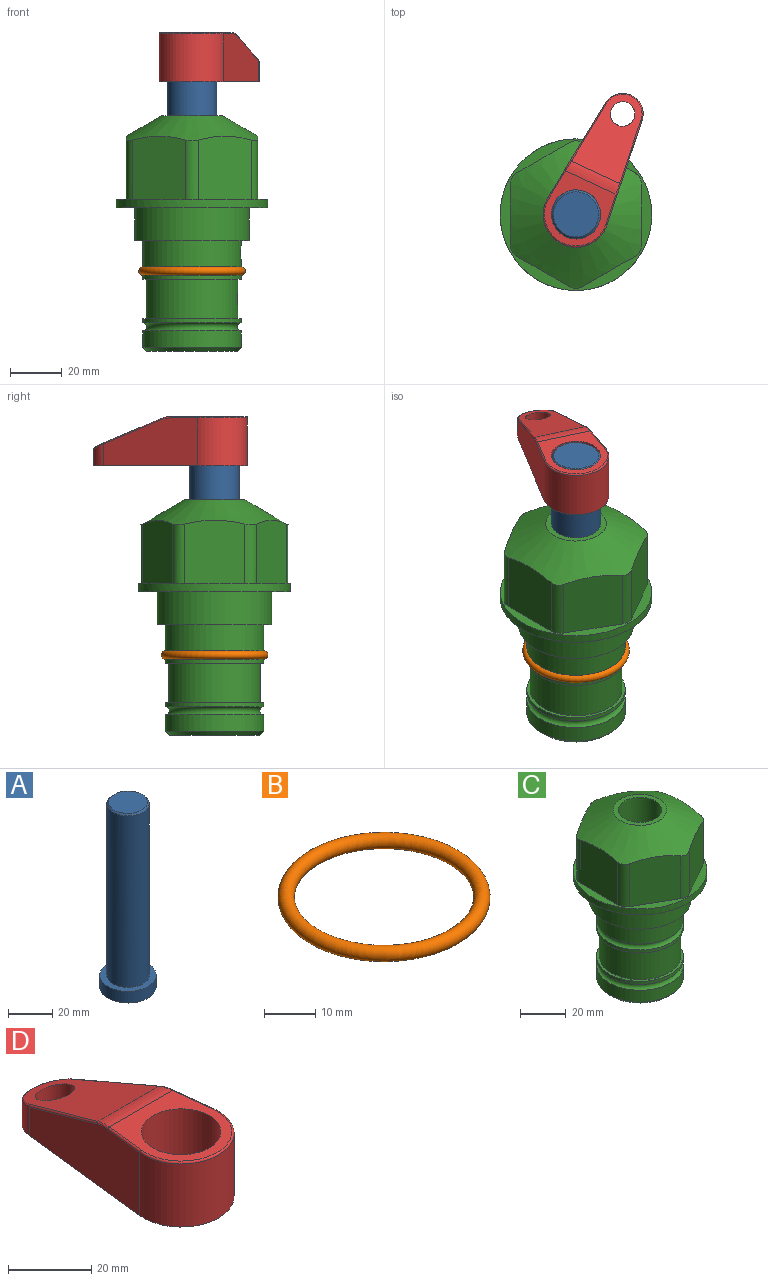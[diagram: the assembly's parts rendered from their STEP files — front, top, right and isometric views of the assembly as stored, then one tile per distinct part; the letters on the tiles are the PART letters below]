
ASSEMBLY  parts=4 mates=2
PART A: 6 faces, bbox 25.4x25.4x101.6 mm
  f0: plane 17.46x17.46mm, normal (0,0,1), area 239.5mm2, adj f5
  f1: plane 25.4x25.4mm, normal (0,0,-1), area 506.7mm2, adj f2
  f2: cylinder r=12.7mm len=25.4mm, axis (0,0,1), area 506.7mm2, adj f1,f3
  f3: plane 25.4x25.4mm, normal (0,0,1), area 221.7mm2, adj f2,f4
  f4: cylinder r=9.53mm len=94.46mm, axis (0,0,1), area 5653mm2, adj f3,f5
  f5: cone r=8.73mm half-angle=45deg, axis (0,0,-1), area 64.4mm2, adj f0,f4
PART B: 1 faces, bbox 44.7x44.7x3.2 mm
  f0: torus R=19.05mm, axis (0,0,1), area 1193.9mm2
PART C: 36 faces, bbox 58.7x58.7x91.2 mm
  f0: cylinder r=17.78mm len=35.56mm, axis (0,0,1), area 1670.8mm2, adj f23,f24,f31
  f1: cylinder r=19.05mm len=38.1mm, axis (0,0,1), area 1191.9mm2, adj f26,f27,f30
  f2: plane 58.66x58.66mm, normal (0,0,-1), area 1150.6mm2, adj f3,f28
  f3: cylinder r=29.33mm len=58.66mm, axis (0,0,-1), area 585.1mm2, adj f2,f4
  f4: plane 58.66x58.66mm, normal (0,0,1), area 475.9mm2, adj f3,f5,f6,f7,f8,f9,f10,f11
  f5: plane 24.5x20.32mm, normal (-0.5,0.87,0), area 562.8mm2, adj f4,f15,f16,f17
  f6: plane 24.5x20.32mm, normal (0.5,0.87,0), area 562.8mm2, adj f4,f14,f15,f17
  f7: plane 24.5x23.48mm, normal (1,0,0), area 562.8mm2, adj f4,f13,f14,f17
  f8: plane 24.5x20.32mm, normal (0.5,-0.87,0), area 562.8mm2, adj f4,f12,f13,f17
  f9: plane 24.5x20.32mm, normal (-0.5,-0.87,0), area 562.8mm2, adj f4,f11,f12,f17
  f10: plane 24.5x23.48mm, normal (-1,0,0), area 562.8mm2, adj f4,f11,f16,f17
  f11: cylinder r=5.08mm len=23.01mm, axis (0,0,-1), area 121.2mm2, adj f4,f9,f10,f17
  f12: cylinder r=5.08mm len=23.01mm, axis (0,0,-1), area 121.2mm2, adj f4,f8,f9,f17
  f13: cylinder r=5.08mm len=23.01mm, axis (0,0,-1), area 121.2mm2, adj f4,f7,f8,f17
  f14: cylinder r=5.08mm len=23.01mm, axis (0,0,-1), area 121.2mm2, adj f4,f6,f7,f17
  f15: cylinder r=5.08mm len=23.01mm, axis (0,0,-1), area 121.2mm2, adj f4,f5,f6,f17
  f16: cylinder r=5.08mm len=23.01mm, axis (0,0,-1), area 121.2mm2, adj f4,f5,f10,f17
  f17: cone r=11.73mm half-angle=60deg, axis (0,0,-1), area 2071.8mm2, adj f5,f6,f7,f8,f9,f10,f11,f12
  f18: plane 23.46x23.46mm, normal (0,0,1), area 147.4mm2, adj f17,f35
  f19: plane 34.93x34.93mm, normal (0,0,-1), area 958mm2, adj f29
  f20: cylinder r=19.05mm len=38.1mm, axis (0,0,1), area 760.1mm2, adj f21,f29
  f21: torus R=19.05mm, axis (0,0,1), area 565.3mm2, adj f20,f22
  f22: cylinder r=19.05mm len=38.1mm, axis (0,0,1), area 190mm2, adj f21,f23
  f23: plane 38.1x38.1mm, normal (0,0,1), area 146.9mm2, adj f0,f22
  f24: plane 38.1x38.1mm, normal (0,0,-1), area 146.9mm2, adj f0,f25
  f25: cylinder r=19.05mm len=38.1mm, axis (0,0,1), area 190mm2, adj f24,f26
  f26: torus R=19.05mm, axis (0,0,1), area 565.3mm2, adj f1,f25
  f27: plane 44.45x44.45mm, normal (0,0,-1), area 411.7mm2, adj f1,f28
  f28: cylinder r=22.23mm len=44.45mm, axis (0,0,1), area 1773.5mm2, adj f2,f27
  f29: cone r=19.05mm half-angle=45deg, axis (0,0,1), area 257.5mm2, adj f19,f20
  f30: cylinder r=3.17mm len=6.75mm, axis (-1,0,0), area 128mm2, adj f1,f33
  f31: cylinder r=3.17mm len=6.35mm, axis (-1,0,0), area 102.5mm2, adj f0,f33
  f32: plane 25.4x25.4mm, normal (0,0,1), area 506.7mm2, adj f33
  f33: cylinder r=12.7mm len=66.42mm, axis (0,0,-1), area 5236.2mm2, adj f30,f31,f32,f34
  f34: cone r=9.53mm half-angle=30deg, axis (0,0,-1), area 443.4mm2, adj f33,f35
  f35: cylinder r=9.53mm len=19.05mm, axis (0,0,-1), area 849mm2, adj f18,f34
PART D: 44 faces, bbox 27.5x64.5x19.1 mm
  f0: plane 2.3x0.95mm, normal (0,0,-1), area 1mm2, adj f25,f30,f34
  f1: plane 63.5x25.4mm, normal (0,0,-1), area 561.7mm2, adj f2,f3,f4,f5,f6,f7,f19,f20
  f2: cylinder r=12.7mm len=25.4mm, axis (0,0,-1), area 792.2mm2, adj f1,f3,f5,f13
  f3: plane 42.33x18.54mm, normal (0.99,0.11,0), area 647mm2, adj f1,f2,f4,f11,f12,f14
  f4: cylinder r=7.94mm len=15.78mm, axis (0,0,-1), area 158.6mm2, adj f1,f3,f5,f16
  f5: plane 42.33x18.54mm, normal (-0.99,0.11,0), area 647mm2, adj f1,f2,f4,f15,f17,f18
  f6: cylinder r=9.53mm len=19.05mm, axis (0,0,-1), area 1140.1mm2, adj f1,f8
  f7: cylinder r=4.76mm len=10.98mm, axis (0,0,-1), area 276.1mm2, adj f1,f9
  f8: plane 25.83x24.38mm, normal (0,0,1), area 262.2mm2, adj f6,f10,f11,f13,f15
  f9: plane 32.49x20.55mm, normal (0,0.34,0.94), area 489.9mm2, adj f7,f10,f14,f16,f18
  f10: cylinder r=12.7mm len=21.49mm, axis (-1,0,0), area 93.2mm2, adj f8,f9,f12,f17
  f11: cylinder r=0.51mm len=12.34mm, axis (0.11,-0.99,0), area 9.9mm2, adj f3,f8,f12,f13
  f12: bspline ~7.62x1.64mm, area 3.5mm2, adj f3,f10,f11,f14
  f13: torus R=12.19mm, axis (0,0,1), area 33.6mm2, adj f2,f8,f11,f15
  f14: cylinder r=0.51mm len=26.01mm, axis (0.1,-0.93,0.34), area 21.6mm2, adj f3,f9,f12,f16
  f15: cylinder r=0.51mm len=12.34mm, axis (0.11,0.99,0), area 9.9mm2, adj f5,f8,f13,f17
  f16: bspline ~15.78x7.05mm, area 15.7mm2, adj f4,f9,f14,f18
  f17: bspline ~7.62x1.64mm, area 3.5mm2, adj f5,f10,f15,f18
  f18: cylinder r=0.51mm len=26.01mm, axis (0.1,0.93,-0.34), area 21.6mm2, adj f5,f9,f16,f17
  f19: plane 21.6x14.29mm, normal (-0.99,-0.11,0), area 242.6mm2, adj f1,f26,f28,f34,f36,f38
  f20: plane 21.6x14.29mm, normal (0.99,-0.11,0), area 242.6mm2, adj f1,f27,f29,f37,f39,f41
  f21: cylinder r=12.7mm len=14.29mm, axis (0,0,-1), area 173.2mm2, adj f1,f26,f27,f30,f31,f33
  f22: cylinder r=7.94mm len=7.63mm, axis (0,0,-1), area 53.8mm2, adj f1,f28,f29,f42
  f23: plane 2.3x0.95mm, normal (0,0,-1), area 1mm2, adj f25,f33,f37
  f24: plane 17.94x12.32mm, normal (0,-0.34,-0.94), area 191.2mm2, adj f25,f38,f41,f42
  f25: cylinder r=9.53mm len=12.93mm, axis (-1,0,0), area 37.5mm2, adj f0,f23,f24,f31,f36,f39
  f26: cylinder r=1.59mm len=14.29mm, axis (0,0,-1), area 49mm2, adj f1,f19,f21,f32
  f27: cylinder r=1.59mm len=14.29mm, axis (0,0,-1), area 49mm2, adj f1,f20,f21,f35
  f28: cylinder r=1.59mm len=7.28mm, axis (0,0,-1), area 22.1mm2, adj f1,f19,f22,f40
  f29: cylinder r=1.59mm len=7.28mm, axis (0,0,-1), area 22.1mm2, adj f1,f20,f22,f43
  f30: torus R=14.29mm, axis (0,0,1), area 5.8mm2, adj f0,f21,f31,f32
  f31: bspline ~11.06x2.73mm, area 20.8mm2, adj f21,f25,f30,f33
  f32: sphere r=1.59mm, area 5.4mm2, adj f26,f30,f34
  f33: torus R=14.29mm, axis (0,0,1), area 5.8mm2, adj f21,f23,f31,f35
  f34: cylinder r=1.59mm len=1.68mm, axis (-0.11,0.99,0), area 2.4mm2, adj f0,f19,f32,f36
  f35: sphere r=1.59mm, area 5.4mm2, adj f27,f33,f37
  f36: bspline ~5.82x2.33mm, area 7.7mm2, adj f19,f25,f34,f38
  f37: cylinder r=1.59mm len=1.68mm, axis (0.11,0.99,0), area 2.4mm2, adj f20,f23,f35,f39
  f38: cylinder r=1.59mm len=18.33mm, axis (0.1,-0.93,0.34), area 46.7mm2, adj f19,f24,f36,f40
  f39: bspline ~5.82x2.33mm, area 7.7mm2, adj f20,f25,f37,f41
  f40: sphere r=1.59mm, area 3.6mm2, adj f28,f38,f42
  f41: cylinder r=1.59mm len=18.33mm, axis (0.1,0.93,-0.34), area 46.7mm2, adj f20,f24,f39,f43
  f42: bspline ~8.31x1.84mm, area 15.3mm2, adj f22,f24,f40,f43
  f43: sphere r=1.59mm, area 3.6mm2, adj f29,f41,f42
PLACE A rot(axis=(0,0,-1),24.9deg) t=(0,0,-5.89)mm
PLACE B at identity
PLACE C at identity fixed
PLACE D rot(axis=(0,0,-1),24.9deg) t=(0,0,48.72)mm
MATE cylindrical A.f2 <-> C.f0  axis (0,0,1) through (0,0,19.75)mm
MATE fastened D.f2 <-> A.f2  axis (0,0,-1) through (0,0,67.77)mm
